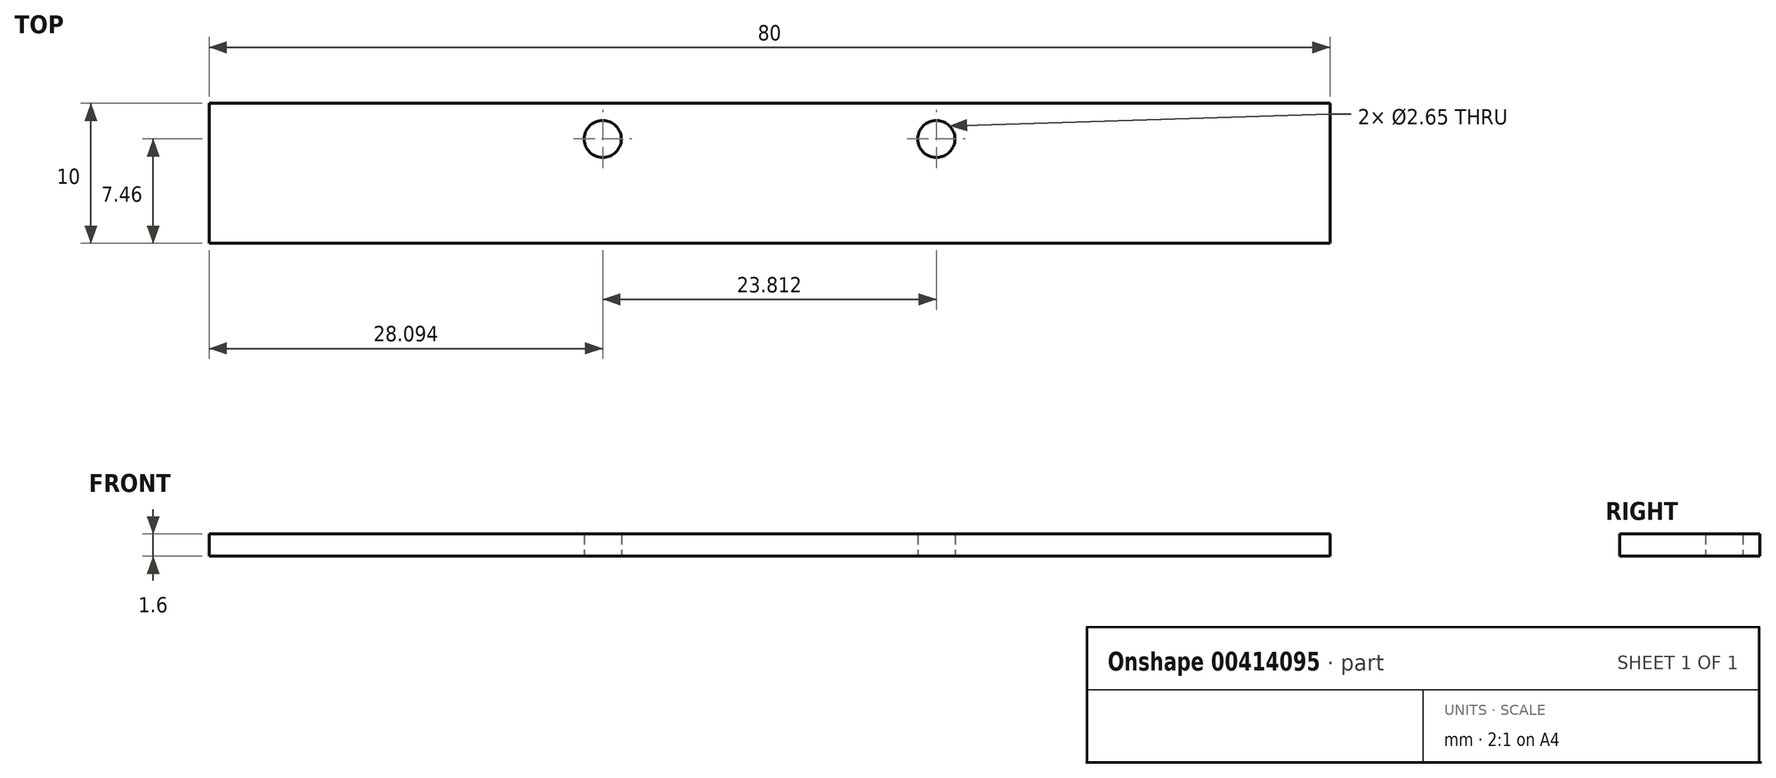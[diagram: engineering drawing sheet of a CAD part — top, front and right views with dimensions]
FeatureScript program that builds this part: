
annotation { "Feature Type Name" : "Feature", "Feature Type Description" : "" }
export const myFeature = defineFeature(function(context is Context, id is Id, definition is map)
    precondition{}
    {
        {
            var Q0;
            Q0=qCreatedBy(makeId("Top.planeOp"),FACE);
            var sketch = newSketch(context, id + "F0", { "sketchPlane" : qUnion([Q0])});
            skLineSegment(sketch, "E0.bottom", {"start": v(0, 0) * mm, "end": v(80, 0) * mm});
            skLineSegment(sketch, "E0.top", {"start": v(0, 10) * mm, "end": v(80, 10) * mm});
            skLineSegment(sketch, "E0.left", {"start": v(0, 0) * mm, "end": v(0, 10) * mm});
            skLineSegment(sketch, "E0.right", {"start": v(80, 0) * mm, "end": v(80, 10) * mm});
            skLineSegment(sketch, "E1.bottom", {"start": v(55.87, 10) * mm, "end": v(24.12, 10) * mm});
            skLineSegment(sketch, "E1.top", {"start": v(55.87, 0) * mm, "end": v(24.12, 0) * mm});
            skPoint(sketch, "E1.middle", {"position": v(40, 5) * mm});
            skPoint(sketch, "E2", {"position": v(32.06, 5) * mm});
            skPoint(sketch, "E3", {"position": v(47.94, 5) * mm});
            skPoint(sketch, "E4", {"position": v(51.9, 5) * mm});
            skPoint(sketch, "E5", {"position": v(28.1, 5) * mm});
            skPoint(sketch, "E6.orphan", {"position": v(40, 10) * mm});
            skPoint(sketch, "E7.orphan", {"position": v(24.12, 5) * mm});
            skPoint(sketch, "E8.end.orphan", {"position": v(40, 0) * mm});
            skPoint(sketch, "E9.orphan", {"position": v(55.87, 5) * mm});
            skLineSegment(sketch, "E10.top", {"start": v(28.1, 7.46) * mm, "end": v(51.9, 7.46) * mm});
            skCircle(sketch, "E11", {"center": v(28.1, 7.46) * mm, "radius": 1.32 * mm});
            skCircle(sketch, "E12", {"center": v(51.9, 7.46) * mm, "radius": 1.32 * mm});
            skSolve(sketch);
        }
        {
            var Q0;
            Q0=makeQuery(id+"F0.imprint","IMPRINT",FACE,{"disambiguationData":[TD([[makeQuery(id+"F0.imprint","IMPRINT",EDGE,{"derivedFrom":sQuery(id+"F0.wireOp",EDGE,"E0.bottom")}),1.0]])]});
            extrude(context, id + "F1", {"entities" : qUnion([Q0]), "depth" : 1.6 * mm});
        }
    });
